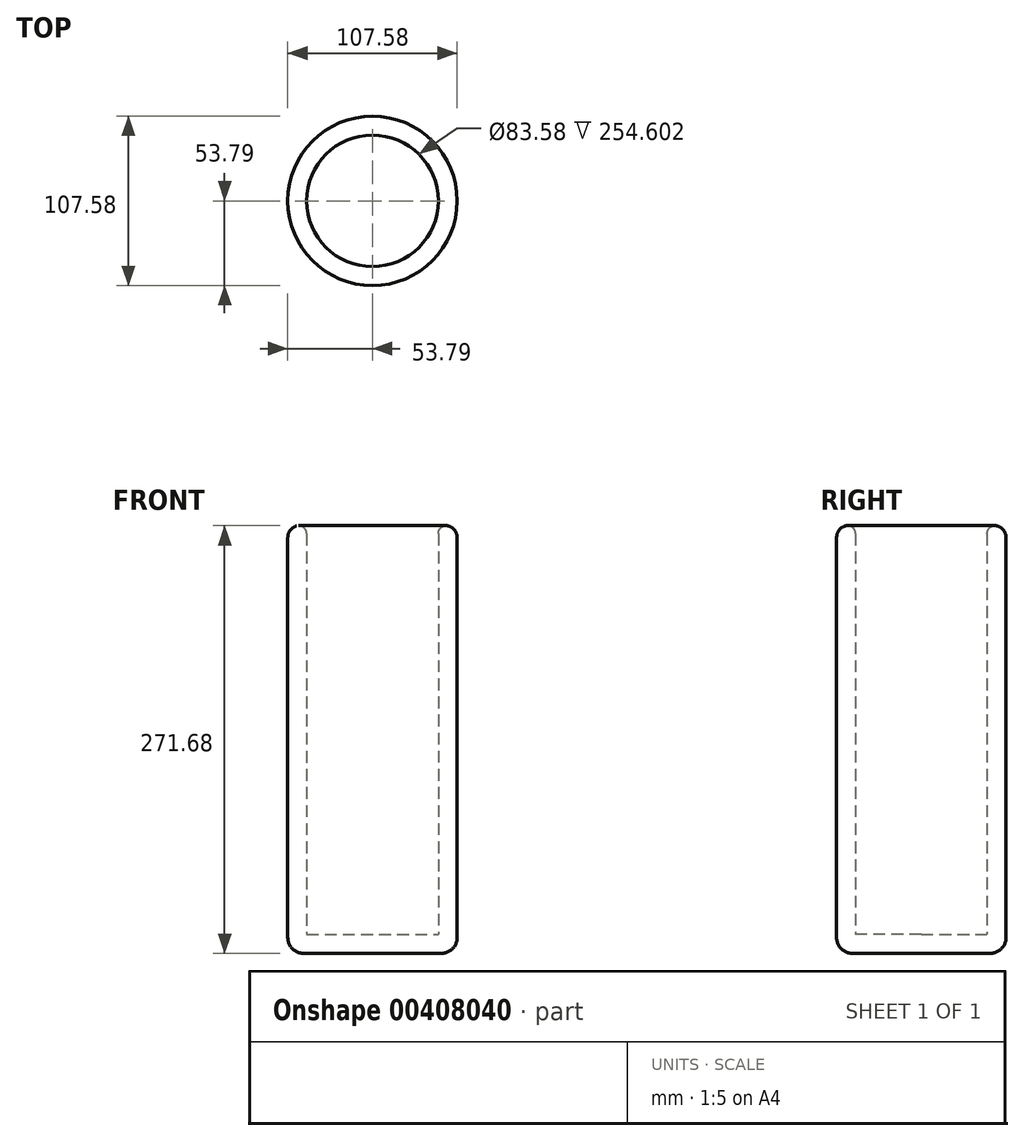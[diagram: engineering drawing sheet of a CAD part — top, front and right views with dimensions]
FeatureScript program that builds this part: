
annotation { "Feature Type Name" : "Feature", "Feature Type Description" : "" }
export const myFeature = defineFeature(function(context is Context, id is Id, definition is map)
    precondition{}
    {
        {
            var Q0;
            Q0=qCreatedBy(makeId("Top.planeOp"),FACE);
            var sketch = newSketch(context, id + "F0", { "sketchPlane" : qUnion([Q0])});
            skCircle(sketch, "E0", {"center": v(0, 0) * mm, "radius": 53.79 * mm});
            skSolve(sketch);
        }
        {
            var Q0;
            Q0=makeQuery(id+"F0.imprint","IMPRINT",FACE,{"disambiguationData":[TD([[makeQuery(id+"F0.imprint","IMPRINT",EDGE,{"derivedFrom":sQuery(id+"F0.wireOp",EDGE,"E0")}),1.0]])]});
            extrude(context, id + "F1", {"entities" : qUnion([Q0]), "depth" : 271.78 * mm});
        }
        {
            var Q0;
            Q0=makeQuery(id+"F1.opExtrude","CAP_FACE",FACE,{"disambiguationData":[OSD([sQuery(id+"F0.wireOp",EDGE,"E0")])],"isStart":false});
            shell(context, id + "F2", {"entities" : qUnion([Q0]), "thickness" : 12 * mm});
        }
        {
            var Q0;
            Q0=makeQuery(id+"F1.opExtrude","CAP_EDGE",EDGE,{"disambiguationData":[OSD([sQuery(id+"F0.wireOp",EDGE,"E0")])],"isStart":false});
            fillet(context, id + "F3", {"entities" : qUnion([Q0]), "radius" : 7.62 * mm, "tangentPropagation" : true, "allowEdgeOverflow" : false});
        }
        {
            var Q0;
            {var subQ0=sQuery(id+"F0.wireOp",EDGE,"E0");Q0=makeQuery(id+"F2.opShell","OFFSET_EDGE",EDGE,{"disambiguationData":[OSD([subQ0]),TDD([makeQuery(id+"F1.opExtrude","CAP_EDGE",EDGE,{"disambiguationData":[OSD([subQ0])],"isStart":false})])]});}
            fillet(context, id + "F4", {"entities" : qUnion([Q0]), "radius" : 5.08 * mm, "tangentPropagation" : true, "allowEdgeOverflow" : false});
        }
        {
            var Q0;
            Q0=makeQuery(id+"F1.opExtrude","CAP_EDGE",EDGE,{"disambiguationData":[OSD([sQuery(id+"F0.wireOp",EDGE,"E0")])],"isStart":true});
            var Q1;
            Q1=makeQuery(id+"F1.opExtrude","SWEPT_FACE",FACE,{"disambiguationData":[OSD([sQuery(id+"F0.wireOp",EDGE,"E0")])]});
            fillet(context, id + "F5", {"entities" : qUnion([Q0, Q1]), "radius" : 10 * mm, "tangentPropagation" : true, "allowEdgeOverflow" : false});
        }
    });
